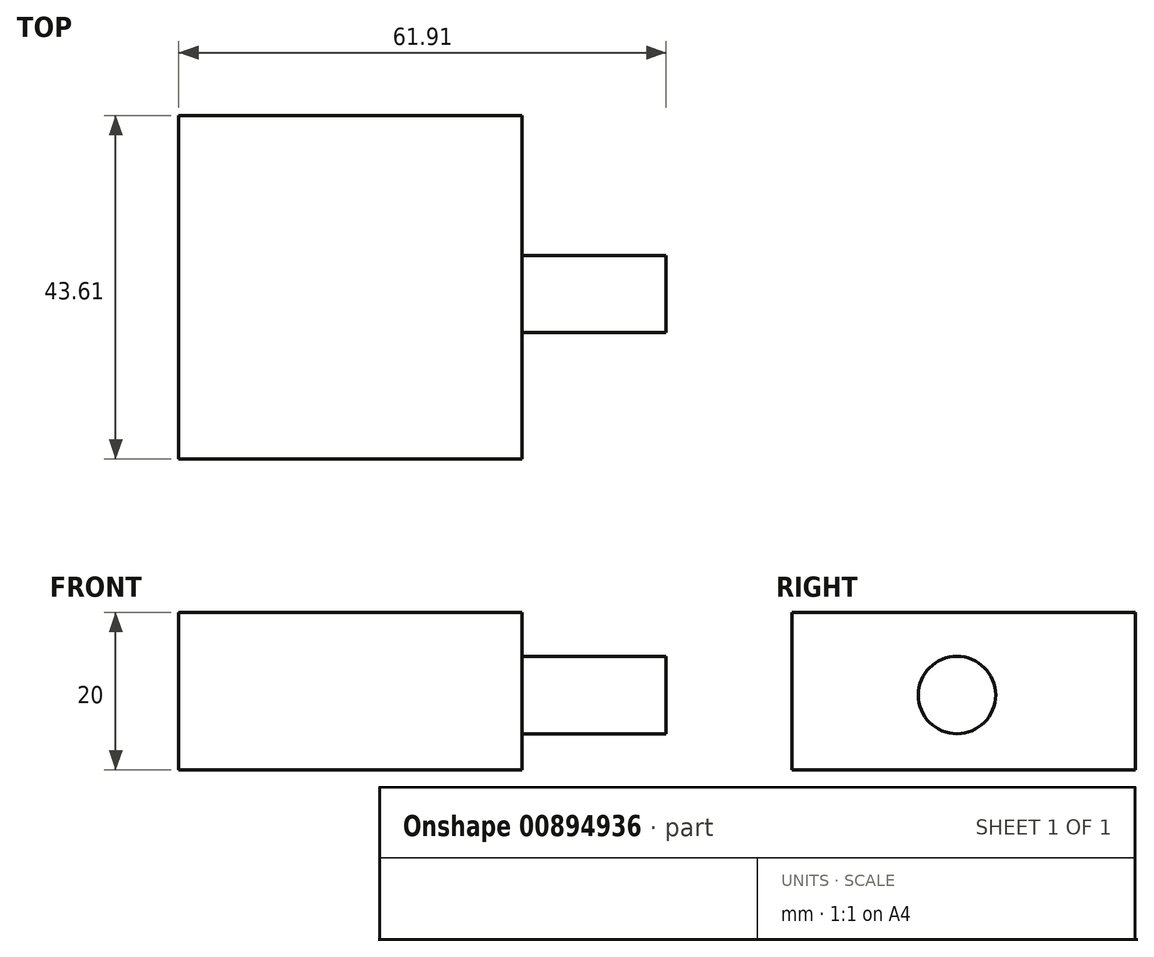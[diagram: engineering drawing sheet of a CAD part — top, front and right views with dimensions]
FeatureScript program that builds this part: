
annotation { "Feature Type Name" : "Feature", "Feature Type Description" : "" }
export const myFeature = defineFeature(function(context is Context, id is Id, definition is map)
    precondition{}
    {
        {
            var Q0;
            Q0=qCreatedBy(makeId("Top.planeOp"),FACE);
            var sketch = newSketch(context, id + "F0", { "sketchPlane" : qUnion([Q0])});
            skLineSegment(sketch, "E0.bottom", {"start": v(0, 0) * mm, "end": v(-43.61, 0) * mm});
            skLineSegment(sketch, "E0.top", {"start": v(0, 43.61) * mm, "end": v(-43.61, 43.61) * mm});
            skLineSegment(sketch, "E0.left", {"start": v(0, 0) * mm, "end": v(0, 43.61) * mm});
            skLineSegment(sketch, "E0.right", {"start": v(-43.61, 0) * mm, "end": v(-43.61, 43.61) * mm});
            skSolve(sketch);
        }
        {
            var Q0;
            Q0=makeQuery(id+"F0.imprint","IMPRINT",FACE,{"disambiguationData":[TD([[makeQuery(id+"F0.imprint","IMPRINT",EDGE,{"derivedFrom":sQuery(id+"F0.wireOp",EDGE,"E0.bottom")}),-1.0]])]});
            extrude(context, id + "F1", {"entities" : qUnion([Q0]), "depth" : 20 * mm, "offsetDistance" : 25 * mm});
        }
        {
            var Q0;
            Q0=qCreatedBy(makeId("Right.planeOp"),FACE);
            var sketch = newSketch(context, id + "F2", { "sketchPlane" : qUnion([Q0])});
            skCircle(sketch, "E1", {"center": v(20.95, 9.5) * mm, "radius": 4.92 * mm});
            skSolve(sketch);
        }
        {
            var Q0;
            Q0 = qSketchRegion(id + "F2", true);
            extrude(context, id + "F3", {"entities" : qUnion([Q0]), "operationType" : NewBodyOperationType.ADD, "depth" : 18.3 * mm, "offsetDistance" : 25 * mm});
        }
    });
